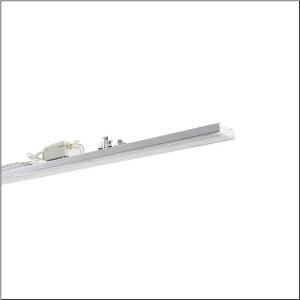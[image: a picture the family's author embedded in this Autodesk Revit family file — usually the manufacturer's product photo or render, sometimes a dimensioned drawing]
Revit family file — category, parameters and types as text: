
# Revit family: licross_r__21_recessed_mo_52tl10mn4a5g_0eff
name_source: partatom
category: Lighting Fixtures
units: mm (PartAtom-declared; Revit-internal decimal feet)

## family parameters
Cut with Voids When Loaded = No
Host = Face
Light Source = No
Part Type = Normal
Room Calculation Point = No
Round Connector Dimension = Use Diameter
Shared = No

## types (1)
- --- (1 x LED, 10690 lm, 60.5 W, 4000K)
    Apparent Load = 61 VA
    CIE Flux Codes = 50 81 96 100 100
    Color Rendering = 80
    Color Temperature = 4000K
    Default Elevation = 1800 mm
    Description = Licross® 21 Recessed MO, luminaire insert, of sheet steel, galvanised, coil coated, white, length: 1.500mm, width: 66mm, height: 67mm, LED rated luminous flux: 10.690lm, light colour: 840, control gear: ON/OFF Multilumen, with plug, 3-pole, with phase selection, mains connection: 220..240V, AC, 50/60Hz, rated input power: 61W, halogen-free wiring, primary optical cover: cover, of PMMA, light emission: direct distribution, primary light characteristic: symmetric, protection rating (complete): IP40, insulation class (complete): insulation class I (protective earthing), certification: CE, ENEC, VDE, UKCA, protection symbol: D if used in an environment without relevant dust loads with corresponding accessories, impact resistance: IK06, permissible ambient temperature for indoor applications: -35..+40°C, corresponds to IFS (International Featured Standards) requirements for safety and quality in the food industry, reducing of maximum allowable ambient temperature of 5°C with ceiling mounting, LABS conformity tested according to VDMA 24364:2018-05, packaging unit: 1 piece
    Height = 58 mm
    Lamp = 1 x LED
    Lamp Light Flux = 10690 lm
    Lamp Power = 60.5 W
    Lamp count = 1
    Length = 1500 mm
    Luminous efficacy = 177 lm/W
    Manufacturer = Siteco
    ModVariant = No
    Model = 52TL10MN4A5G
    Mounting Place = Ceiling
    Mounting Type = Pendant
    Number of Poles = 1
    OnlyDefault = Yes
    Power Factor = 1
    Product Name = Licross® 21 Recessed MO
    Product group = luminaire insert
    ProductGroupID = 901
    Protection Class = Protection class I
    Protection Degree = IP 40
    RLX_Detail_Level = 1
    RLX_Emergency_Light_Flux = 0 lm
    RLX_Emergency_Type = 0
    RLX_Emergency_Type_DB = No
    RlxData = <blob elided: 22109 chars, md5=ccb395ec>
    Socket = socket
    Standby Power = 0 W
    System Light Flux = 10690 lm
    System Power = 61 W
    Type Comments = factory setting: luminous flux: 100 % | (A | C | E) | 140 mA
    Type Image = l_1296930.jpg
    URL = http://relux.com
    VarID = @adj_038209
    Voltage = 0 V
    Weight = 0.00 kg
    Width = 66 mm

## geometry (parser evidence)
native form markers: Blend x4, Sweep x12
no freeform markers — native parametric forms only
